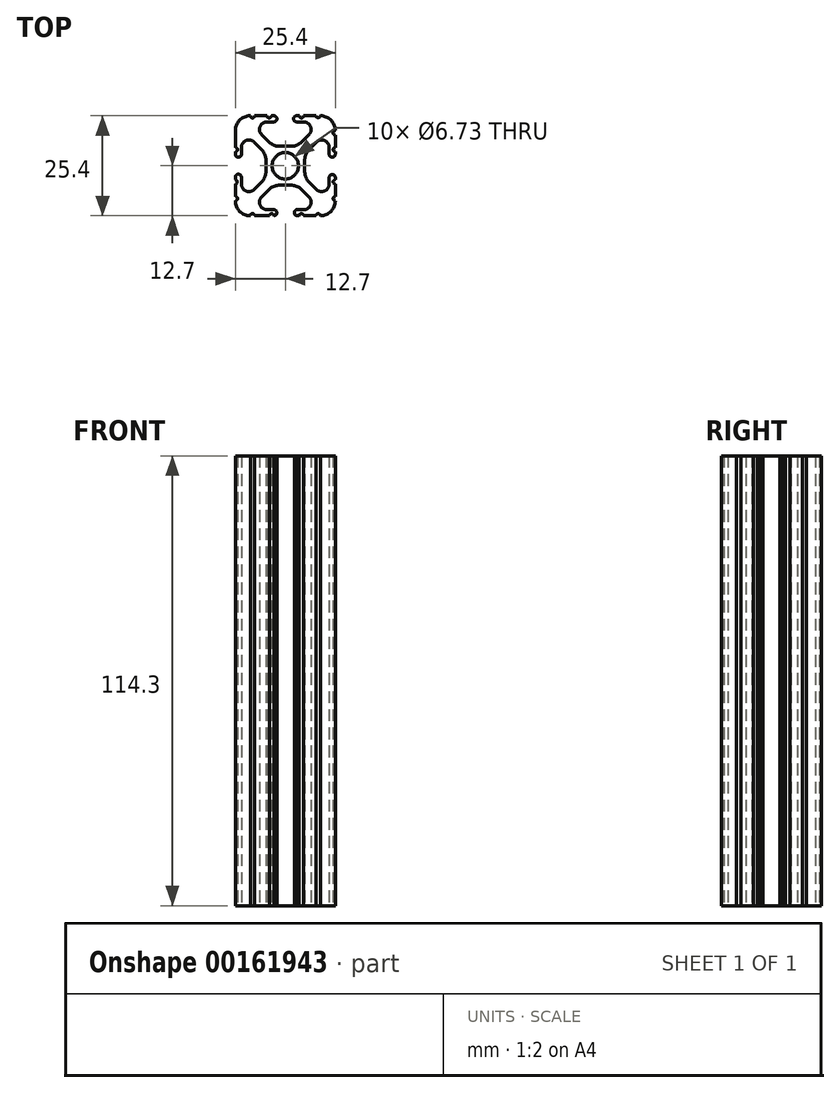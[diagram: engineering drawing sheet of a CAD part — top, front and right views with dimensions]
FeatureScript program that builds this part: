
annotation { "Feature Type Name" : "Feature", "Feature Type Description" : "" }
export const myFeature = defineFeature(function(context is Context, id is Id, definition is map)
    precondition{}
    {
        {
            var Q0;
            Q0=qCreatedBy(makeId("Top.planeOp"),FACE);
            var sketch = newSketch(context, id + "F0", { "sketchPlane" : qUnion([Q0])});
            skCircle(sketch, "E0", {"center": v(-12.7, 12.7) * mm, "radius": 3.36 * mm});
            skLineSegment(sketch, "E1.bottom", {"start": v(-11.24, 17.64) * mm, "end": v(-14.16, 17.64) * mm});
            skLineSegment(sketch, "E1.top", {"start": v(-11.24, 7.76) * mm, "end": v(-14.16, 7.76) * mm});
            skLineSegment(sketch, "E1.left", {"start": v(-7.76, 14.16) * mm, "end": v(-7.76, 11.24) * mm});
            skLineSegment(sketch, "E1.right", {"start": v(-17.64, 14.16) * mm, "end": v(-17.64, 11.24) * mm});
            skPoint(sketch, "E2.visualSharp", {"position": v(-25.4, 25.4) * mm});
            skPoint(sketch, "E3.visualSharp", {"position": v(0, 25.4) * mm});
            skPoint(sketch, "E4.visualSharp", {"position": v(0, 0) * mm});
            skPoint(sketch, "E5.visualSharp", {"position": v(-25.4, 0) * mm});
            skLineSegment(sketch, "E6.0", {"start": v(-18.7, 20.6) * mm, "end": v(-16.85, 18.76) * mm});
            skLineSegment(sketch, "E7.0", {"start": v(-20.6, 18.7) * mm, "end": v(-18.76, 16.85) * mm});
            skPoint(sketch, "E8.orphan", {"position": v(-23.85, 1.55) * mm});
            skPoint(sketch, "E9.orphan", {"position": v(-23.85, 23.85) * mm});
            skPoint(sketch, "E10.orphan", {"position": v(-1.55, 23.85) * mm});
            skPoint(sketch, "E11.orphan", {"position": v(-1.55, 1.55) * mm});
            skLineSegment(sketch, "E12", {"start": v(-8.55, 6.64) * mm, "end": v(-6.7, 4.8) * mm});
            skLineSegment(sketch, "E13.0", {"start": v(-18.7, 4.8) * mm, "end": v(-16.85, 6.64) * mm});
            skLineSegment(sketch, "E14.0", {"start": v(-20.6, 6.7) * mm, "end": v(-18.76, 8.55) * mm});
            skLineSegment(sketch, "E15.0", {"start": v(-8.55, 18.76) * mm, "end": v(-6.7, 20.6) * mm});
            skPoint(sketch, "E16.visualSharp", {"position": v(-23.85, 21.95) * mm});
            skArc(sketch, "E16.filletArc", {"start": v(-20.6, 18.7) * mm, "mid": v(-22.68, 19.1) * mm, "end": v(-23.85, 17.35) * mm});
            skPoint(sketch, "E17.visualSharp", {"position": v(-21.95, 23.85) * mm});
            skArc(sketch, "E17.filletArc", {"start": v(-17.35, 23.85) * mm, "mid": v(-19.1, 22.68) * mm, "end": v(-18.7, 20.6) * mm});
            skPoint(sketch, "E18.visualSharp", {"position": v(-5.34, 23.85) * mm});
            skLineSegment(sketch, "E19", {"start": v(-17.35, 23.85) * mm, "end": v(-15.58, 23.85) * mm});
            skLineSegment(sketch, "E20", {"start": v(-23.85, 17.35) * mm, "end": v(-23.85, 15.62) * mm});
            skLineSegment(sketch, "E21", {"start": v(-8.05, 1.55) * mm, "end": v(-9.78, 1.55) * mm});
            skArc(sketch, "E22.filletArc", {"start": v(-6.7, 20.6) * mm, "mid": v(-6.3, 22.68) * mm, "end": v(-8.05, 23.85) * mm});
            skPoint(sketch, "E23.visualSharp", {"position": v(-1.55, 3.45) * mm});
            skPoint(sketch, "E24.visualSharp", {"position": v(-3.45, 1.55) * mm});
            skArc(sketch, "E24.filletArc", {"start": v(-8.05, 1.55) * mm, "mid": v(-6.3, 2.73) * mm, "end": v(-6.7, 4.8) * mm});
            skArc(sketch, "E25.filletArc", {"start": v(-18.7, 4.8) * mm, "mid": v(-19.1, 2.73) * mm, "end": v(-17.35, 1.55) * mm});
            skArc(sketch, "E26.filletArc", {"start": v(-23.85, 8.05) * mm, "mid": v(-22.68, 6.3) * mm, "end": v(-20.6, 6.7) * mm});
            skLineSegment(sketch, "E27.bottom", {"start": v(-4.9, 0) * mm, "end": v(-8.05, 0) * mm});
            skLineSegment(sketch, "E27.top", {"start": v(-4.92, 25.4) * mm, "end": v(-8.05, 25.4) * mm});
            skLineSegment(sketch, "E27.left", {"start": v(0, 4.9) * mm, "end": v(0, 8.05) * mm});
            skLineSegment(sketch, "E27.right", {"start": v(-25.4, 4.9) * mm, "end": v(-25.4, 8.05) * mm});
            skArc(sketch, "E28.filletArc", {"start": v(-25.4, 3.81) * mm, "mid": v(-24.28, 1.12) * mm, "end": v(-21.59, 0) * mm});
            skArc(sketch, "E29.filletArc", {"start": v(-3.81, 0) * mm, "mid": v(-1.12, 1.12) * mm, "end": v(0, 3.8) * mm});
            skArc(sketch, "E30.filletArc", {"start": v(0, 21.59) * mm, "mid": v(-1.12, 24.28) * mm, "end": v(-3.8, 25.4) * mm});
            skArc(sketch, "E31.filletArc", {"start": v(-21.59, 25.4) * mm, "mid": v(-24.28, 24.28) * mm, "end": v(-25.4, 21.59) * mm});
            skPoint(sketch, "E32.newPointA", {"position": v(-17.64, 7.76) * mm});
            skArc(sketch, "E32.filletArc", {"start": v(-14.16, 7.76) * mm, "mid": v(-15.62, 7.47) * mm, "end": v(-16.85, 6.64) * mm});
            skPoint(sketch, "E33.newPointA", {"position": v(-7.76, 7.76) * mm});
            skArc(sketch, "E33.filletArc", {"start": v(-8.55, 6.64) * mm, "mid": v(-9.78, 7.47) * mm, "end": v(-11.24, 7.76) * mm});
            skArc(sketch, "E34.filletArc", {"start": v(-7.76, 11.24) * mm, "mid": v(-7.47, 9.78) * mm, "end": v(-6.64, 8.55) * mm});
            skArc(sketch, "E35.filletArc", {"start": v(-6.64, 16.85) * mm, "mid": v(-7.47, 15.62) * mm, "end": v(-7.76, 14.16) * mm});
            skPoint(sketch, "E36.newPointB", {"position": v(-7.76, 17.64) * mm});
            skArc(sketch, "E36.filletArc", {"start": v(-11.24, 17.64) * mm, "mid": v(-9.78, 17.93) * mm, "end": v(-8.55, 18.76) * mm});
            skPoint(sketch, "E37.newPointB", {"position": v(-17.64, 17.64) * mm});
            skArc(sketch, "E37.filletArc", {"start": v(-16.85, 18.76) * mm, "mid": v(-15.62, 17.93) * mm, "end": v(-14.16, 17.64) * mm});
            skArc(sketch, "E38.filletArc", {"start": v(-17.64, 14.16) * mm, "mid": v(-17.93, 15.62) * mm, "end": v(-18.76, 16.85) * mm});
            skArc(sketch, "E39.filletArc", {"start": v(-18.76, 8.55) * mm, "mid": v(-17.93, 9.78) * mm, "end": v(-17.64, 11.24) * mm});
            skLineSegment(sketch, "E40", {"start": v(-6.64, 8.55) * mm, "end": v(-4.8, 6.7) * mm});
            skPoint(sketch, "E41.visualSharp", {"position": v(-1.55, 21.95) * mm});
            skArc(sketch, "E42.filletArc", {"start": v(-4.8, 6.7) * mm, "mid": v(-2.73, 6.3) * mm, "end": v(-1.55, 8.05) * mm});
            skLineSegment(sketch, "E43", {"start": v(-1.55, 8.05) * mm, "end": v(-1.55, 9.78) * mm});
            skLineSegment(sketch, "E44", {"start": v(-6.64, 16.85) * mm, "end": v(-4.8, 18.7) * mm});
            skArc(sketch, "E45.filletArc", {"start": v(-1.55, 17.35) * mm, "mid": v(-2.73, 19.1) * mm, "end": v(-4.8, 18.7) * mm});
            skArc(sketch, "E46", {"start": v(-23.85, 9.78) * mm, "mid": v(-24.63, 10.56) * mm, "end": v(-25.4, 9.78) * mm});
            skArc(sketch, "E47", {"start": v(-25.4, 15.62) * mm, "mid": v(-24.63, 14.86) * mm, "end": v(-23.85, 15.62) * mm});
            skArc(sketch, "E48", {"start": v(-15.62, 23.85) * mm, "mid": v(-14.83, 24.63) * mm, "end": v(-15.62, 25.4) * mm});
            skArc(sketch, "E49", {"start": v(-9.78, 25.4) * mm, "mid": v(-10.6, 24.63) * mm, "end": v(-9.78, 23.85) * mm});
            skArc(sketch, "E50", {"start": v(-1.55, 15.62) * mm, "mid": v(-0.77, 14.88) * mm, "end": v(0, 15.62) * mm});
            skArc(sketch, "E51", {"start": v(0, 9.78) * mm, "mid": v(-0.77, 10.5) * mm, "end": v(-1.55, 9.78) * mm});
            skArc(sketch, "E52", {"start": v(-9.78, 1.55) * mm, "mid": v(-10.4, 0.77) * mm, "end": v(-9.78, 0) * mm});
            skArc(sketch, "E53", {"start": v(-15.62, 0) * mm, "mid": v(-14.85, 0.77) * mm, "end": v(-15.62, 1.55) * mm});
            skLineSegment(sketch, "E54.trimOffspring", {"start": v(-15.62, 1.55) * mm, "end": v(-17.35, 1.55) * mm});
            skLineSegment(sketch, "E55.trimOffspring", {"start": v(-16.7, 0) * mm, "end": v(-20.5, 0) * mm});
            skLineSegment(sketch, "E56.trimOffspring", {"start": v(-1.55, 15.62) * mm, "end": v(-1.55, 17.35) * mm});
            skLineSegment(sketch, "E57.trimOffspring", {"start": v(0, 15.62) * mm, "end": v(0, 16.26) * mm});
            skLineSegment(sketch, "E58.trimOffspring", {"start": v(-23.85, 9.78) * mm, "end": v(-23.85, 8.05) * mm});
            skLineSegment(sketch, "E59.trimOffspring", {"start": v(-25.4, 15.62) * mm, "end": v(-25.4, 16.26) * mm});
            skLineSegment(sketch, "E60.trimOffspring", {"start": v(-9.86, 23.85) * mm, "end": v(-8.05, 23.85) * mm});
            skLineSegment(sketch, "E61.trimOffspring", {"start": v(-15.58, 25.4) * mm, "end": v(-16.25, 25.4) * mm});
            skPoint(sketch, "E62.start.orphan", {"position": v(-15.62, 17.93) * mm});
            skPoint(sketch, "E63.start.orphan", {"position": v(-9.78, 17.93) * mm});
            skPoint(sketch, "E64.start.orphan", {"position": v(-7.47, 15.62) * mm});
            skPoint(sketch, "E65.start.orphan", {"position": v(-7.47, 9.78) * mm});
            skPoint(sketch, "E66.start.orphan", {"position": v(-17.93, 15.62) * mm});
            skPoint(sketch, "E67.start.orphan", {"position": v(-17.93, 9.78) * mm});
            skPoint(sketch, "E68.start.orphan", {"position": v(-9.78, 7.47) * mm});
            skPoint(sketch, "E69.start.orphan", {"position": v(-15.62, 7.47) * mm});
            skPoint(sketch, "E70.endSnap0", {"position": v(0, 18.6) * mm});
            skPoint(sketch, "E71.startSnap0", {"position": v(-1.55, 8.92) * mm});
            skArc(sketch, "E72", {"start": v(-4.92, 25.4) * mm, "mid": v(-4.37, 24.9) * mm, "end": v(-3.81, 25.4) * mm});
            skArc(sketch, "E73", {"start": v(-9.14, 25.4) * mm, "mid": v(-8.6, 24.86) * mm, "end": v(-8.05, 25.4) * mm});
            skArc(sketch, "E74", {"start": v(-17.35, 25.4) * mm, "mid": v(-16.8, 24.86) * mm, "end": v(-16.25, 25.4) * mm});
            skArc(sketch, "E75", {"start": v(-21.59, 25.4) * mm, "mid": v(-21.04, 24.85) * mm, "end": v(-20.49, 25.4) * mm});
            skLineSegment(sketch, "E76", {"start": v(-25.4, 21.59) * mm, "end": v(-25.4, 20.5) * mm});
            skArc(sketch, "E77", {"start": v(-25.4, 16.26) * mm, "mid": v(-24.84, 16.8) * mm, "end": v(-25.4, 17.35) * mm});
            skArc(sketch, "E78", {"start": v(-25.4, 8.05) * mm, "mid": v(-24.9, 8.6) * mm, "end": v(-25.4, 9.15) * mm});
            skArc(sketch, "E79", {"start": v(-25.4, 3.81) * mm, "mid": v(-24.85, 4.36) * mm, "end": v(-25.4, 4.9) * mm});
            skArc(sketch, "E80", {"start": v(-20.5, 0) * mm, "mid": v(-21.04, 0.55) * mm, "end": v(-21.59, 0) * mm});
            skArc(sketch, "E81", {"start": v(-15.62, 0) * mm, "mid": v(-16.16, 0.54) * mm, "end": v(-16.7, 0) * mm});
            skArc(sketch, "E82", {"start": v(-8.05, 0) * mm, "mid": v(-8.6, 0.55) * mm, "end": v(-9.15, 0) * mm});
            skArc(sketch, "E83", {"start": v(-3.81, 0) * mm, "mid": v(-4.35, 0.54) * mm, "end": v(-4.9, 0) * mm});
            skLineSegment(sketch, "E84.trimOffspring", {"start": v(-17.35, 25.4) * mm, "end": v(-20.49, 25.4) * mm});
            skLineSegment(sketch, "E85.trimOffspring", {"start": v(-25.4, 17.35) * mm, "end": v(-25.4, 21.59) * mm});
            skLineSegment(sketch, "E86.trimOffspring", {"start": v(-25.4, 9.15) * mm, "end": v(-25.4, 9.78) * mm});
            skLineSegment(sketch, "E87.trimOffspring", {"start": v(-9.15, 0) * mm, "end": v(-9.78, 0) * mm});
            skArc(sketch, "E88", {"start": v(0, 4.9) * mm, "mid": v(-0.54, 4.36) * mm, "end": v(0, 3.8) * mm});
            skArc(sketch, "E89", {"start": v(0, 9.15) * mm, "mid": v(-0.54, 8.6) * mm, "end": v(0, 8.05) * mm});
            skLineSegment(sketch, "E90.trimOffspring", {"start": v(0, 9.15) * mm, "end": v(0, 9.78) * mm});
            skArc(sketch, "E91", {"start": v(0, 21.59) * mm, "mid": v(-0.55, 21.04) * mm, "end": v(0, 20.5) * mm});
            skArc(sketch, "E92", {"start": v(0, 17.35) * mm, "mid": v(-0.55, 16.8) * mm, "end": v(0, 16.26) * mm});
            skLineSegment(sketch, "E93.trimOffspring", {"start": v(0, 17.35) * mm, "end": v(0, 20.5) * mm});
            skLineSegment(sketch, "E94.trimOffspring", {"start": v(-9.14, 25.4) * mm, "end": v(-9.86, 25.4) * mm});
            skSolve(sketch);
        }
        {
            var Q0;
            Q0=qSketchRegion(id+"F0",true);
            extrude(context, id + "F1", {"entities" : qUnion([Q0]), "depth" : 114.3 * mm});
        }
    });
